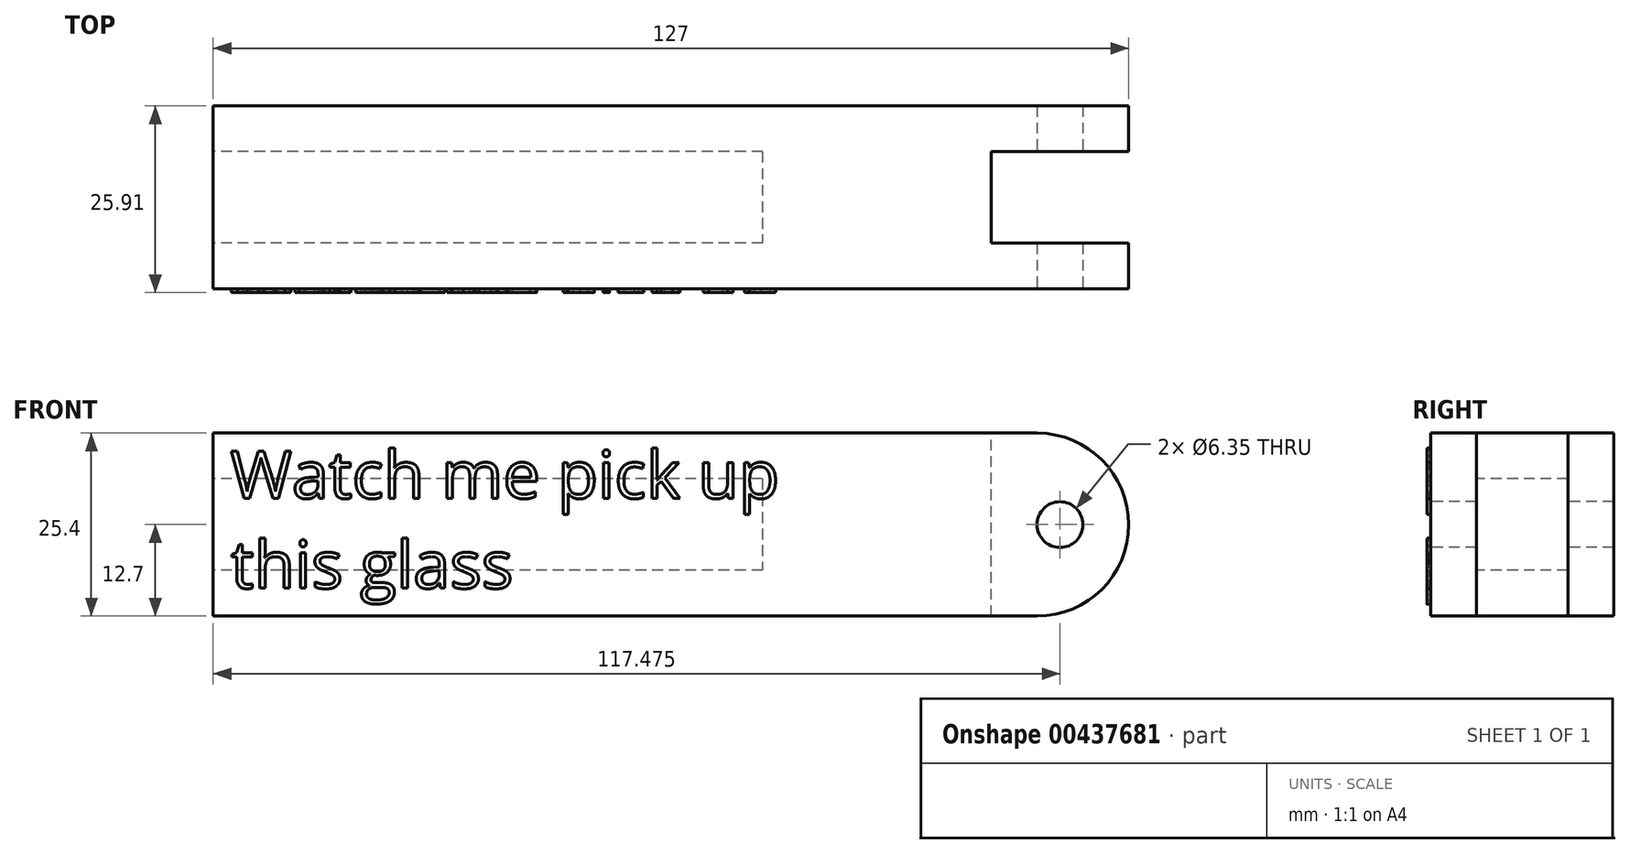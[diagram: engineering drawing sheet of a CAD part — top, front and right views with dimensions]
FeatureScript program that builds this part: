
annotation { "Feature Type Name" : "Feature", "Feature Type Description" : "" }
export const myFeature = defineFeature(function(context is Context, id is Id, definition is map)
    precondition{}
    {
        {
            var Q0;
            Q0=qCreatedBy(makeId("Right.planeOp"),FACE);
            var sketch = newSketch(context, id + "F0", { "sketchPlane" : qUnion([Q0])});
            skLineSegment(sketch, "E0.bottom", {"start": v(-12.7, 12.7) * mm, "end": v(12.7, 12.7) * mm});
            skLineSegment(sketch, "E0.top", {"start": v(-12.7, -12.7) * mm, "end": v(12.7, -12.7) * mm});
            skLineSegment(sketch, "E0.left", {"start": v(-12.7, 12.7) * mm, "end": v(-12.7, -12.7) * mm});
            skLineSegment(sketch, "E0.right", {"start": v(12.7, 12.7) * mm, "end": v(12.7, -12.7) * mm});
            skPoint(sketch, "E0.middle", {"position": v(0, 0) * mm});
            skSolve(sketch);
        }
        {
            var Q0;
            Q0=makeQuery(id+"F0.imprint","IMPRINT",FACE,{"disambiguationData":[TD([[makeQuery(id+"F0.imprint","IMPRINT",EDGE,{"derivedFrom":sQuery(id+"F0.wireOp",EDGE,"E0.bottom")}),-1.0]])]});
            extrude(context, id + "F1", {"entities" : qUnion([Q0]), "depth" : 127 * mm});
        }
        {
            var Q0;
            Q0=makeQuery(id+"F1.opExtrude","SWEPT_FACE",FACE,{"disambiguationData":[OSD([sQuery(id+"F0.wireOp",EDGE,"E0.bottom")])]});
            var sketch = newSketch(context, id + "F2", { "sketchPlane" : qUnion([Q0])});
            skLineSegment(sketch, "E1.bottom", {"start": v(107.95, 6.35) * mm, "end": v(146.05, 6.35) * mm});
            skLineSegment(sketch, "E1.top", {"start": v(107.95, -6.35) * mm, "end": v(146.05, -6.35) * mm});
            skLineSegment(sketch, "E1.left", {"start": v(107.95, 6.35) * mm, "end": v(107.95, -6.35) * mm});
            skLineSegment(sketch, "E1.right", {"start": v(146.05, 6.35) * mm, "end": v(146.05, -6.35) * mm});
            skPoint(sketch, "E1.middle", {"position": v(127, 0) * mm});
            skSolve(sketch);
        }
        {
            var Q0;
            {var subQ0=sQuery(id+"F2.wireOp",EDGE,"E1.left");Q0=makeQuery(id+"F2.imprint","IMPRINT",FACE,{"disambiguationData":[TD([[makeQuery(id+"F2.imprint","IMPRINT",EDGE,{"derivedFrom":subQ0}),1.0]])]});}
            extrude(context, id + "F3", {"entities" : qUnion([Q0]), "operationType" : NewBodyOperationType.REMOVE, "oppositeDirection" : true, "depth" : 25.4 * mm});
        }
        {
            var Q0;
            Q0=makeQuery(id+"F1.opExtrude","SWEPT_FACE",FACE,{"disambiguationData":[OSD([sQuery(id+"F0.wireOp",EDGE,"E0.left")])]});
            var sketch = newSketch(context, id + "F4", { "sketchPlane" : qUnion([Q0])});
            skCircle(sketch, "E2", {"center": v(117.47, 0) * mm, "radius": 3.18 * mm});
            skSolve(sketch);
        }
        {
            var Q0;
            {var subQ0=sQuery(id+"F0.wireOp",EDGE,"E0.bottom");var subQ1=sQuery(id+"F0.wireOp",EDGE,"E0.left");Q0=makeQuery(id+"F3.boolean.opBoolean","SPLIT",EDGE,{"disambiguationData":[TD([makeQuery(id+"F1.opExtrude","SWEPT_FACE",FACE,{"disambiguationData":[OSD([subQ1])]})])],"derivedFrom":makeQuery(id+"F1.opExtrude","CAP_EDGE",EDGE,{"disambiguationData":[OSD([subQ0])],"isStart":false})});}
            var Q1;
            {var subQ0=sQuery(id+"F0.wireOp",EDGE,"E0.left");var subQ1=sQuery(id+"F0.wireOp",EDGE,"E0.top");Q1=makeQuery(id+"F3.boolean.opBoolean","SPLIT",EDGE,{"disambiguationData":[TD([makeQuery(id+"F1.opExtrude","SWEPT_FACE",FACE,{"disambiguationData":[OSD([subQ0])]})])],"derivedFrom":makeQuery(id+"F1.opExtrude","CAP_EDGE",EDGE,{"disambiguationData":[OSD([subQ1])],"isStart":false})});}
            var Q2;
            {var subQ0=sQuery(id+"F0.wireOp",EDGE,"E0.bottom");var subQ1=sQuery(id+"F0.wireOp",EDGE,"E0.right");Q2=makeQuery(id+"F3.boolean.opBoolean","SPLIT",EDGE,{"disambiguationData":[TD([makeQuery(id+"F1.opExtrude","SWEPT_FACE",FACE,{"disambiguationData":[OSD([subQ1])]})])],"derivedFrom":makeQuery(id+"F1.opExtrude","CAP_EDGE",EDGE,{"disambiguationData":[OSD([subQ0])],"isStart":false})});}
            var Q3;
            {var subQ0=sQuery(id+"F0.wireOp",EDGE,"E0.right");var subQ1=sQuery(id+"F0.wireOp",EDGE,"E0.top");Q3=makeQuery(id+"F3.boolean.opBoolean","SPLIT",EDGE,{"disambiguationData":[TD([makeQuery(id+"F1.opExtrude","SWEPT_FACE",FACE,{"disambiguationData":[OSD([subQ0])]})])],"derivedFrom":makeQuery(id+"F1.opExtrude","CAP_EDGE",EDGE,{"disambiguationData":[OSD([subQ1])],"isStart":false})});}
            fillet(context, id + "F5", {"entities" : qUnion([Q0, Q1, Q2, Q3]), "radius" : 12.7 * mm, "tangentPropagation" : true, "allowEdgeOverflow" : false});
        }
        {
            var Q0;
            Q0=makeQuery(id+"F4.imprint","IMPRINT",FACE,{"disambiguationData":[TD([[makeQuery(id+"F4.imprint","IMPRINT",EDGE,{"derivedFrom":sQuery(id+"F4.wireOp",EDGE,"E2")}),1.0]])]});
            extrude(context, id + "F6", {"entities" : qUnion([Q0]), "operationType" : NewBodyOperationType.REMOVE, "oppositeDirection" : true, "depth" : 29.3 * mm});
        }
        {
            var Q0;
            Q0=makeQuery(id+"F1.opExtrude","CAP_FACE",FACE,{"disambiguationData":[OSD([sQuery(id+"F0.wireOp",EDGE,"E0.bottom"),sQuery(id+"F0.wireOp",EDGE,"E0.top"),sQuery(id+"F0.wireOp",EDGE,"E0.left"),sQuery(id+"F0.wireOp",EDGE,"E0.right")])],"isStart":true});
            var sketch = newSketch(context, id + "F7", { "sketchPlane" : qUnion([Q0])});
            skLineSegment(sketch, "E3.bottom", {"start": v(-6.35, 6.35) * mm, "end": v(6.35, 6.35) * mm});
            skLineSegment(sketch, "E3.top", {"start": v(-6.35, -6.35) * mm, "end": v(6.35, -6.35) * mm});
            skLineSegment(sketch, "E3.left", {"start": v(-6.35, 6.35) * mm, "end": v(-6.35, -6.35) * mm});
            skLineSegment(sketch, "E3.right", {"start": v(6.35, 6.35) * mm, "end": v(6.35, -6.35) * mm});
            skPoint(sketch, "E3.middle", {"position": v(0, 0) * mm});
            skSolve(sketch);
        }
        {
            var Q0;
            Q0=makeQuery(id+"F7.imprint","IMPRINT",FACE,{"disambiguationData":[TD([[makeQuery(id+"F7.imprint","IMPRINT",EDGE,{"derivedFrom":sQuery(id+"F7.wireOp",EDGE,"E3.bottom")}),-1.0]])]});
            extrude(context, id + "F8", {"entities" : qUnion([Q0]), "operationType" : NewBodyOperationType.REMOVE, "oppositeDirection" : true, "depth" : 76.2 * mm});
        }
        {
            var Q0;
            Q0=makeQuery(id+"F1.opExtrude","SWEPT_FACE",FACE,{"disambiguationData":[OSD([sQuery(id+"F0.wireOp",EDGE,"E0.left")])]});
            var sketch = newSketch(context, id + "F9", { "sketchPlane" : qUnion([Q0])});
            skText(sketch, "E4", { "text": "Watch me pick up \nthis glass\n", "fontName": "OpenSans-Regular.ttf"});
            skPoint(sketch, "E4.firstSnap0", {"position": v(57.15, -12.7) * mm});
            const initialGuessF9  = {"E4": [0.00243, 0.00366, 1, 0, 0.00661]};
            skSetInitialGuess(sketch, initialGuessF9);
            skSolve(sketch);
        }
        {
            var Q0;
            Q0 = qSketchRegion(id + "F9", true);
            extrude(context, id + "F10", {"entities" : qUnion([Q0]), "operationType" : NewBodyOperationType.ADD, "depth" : 0.5 * mm});
        }
    });
